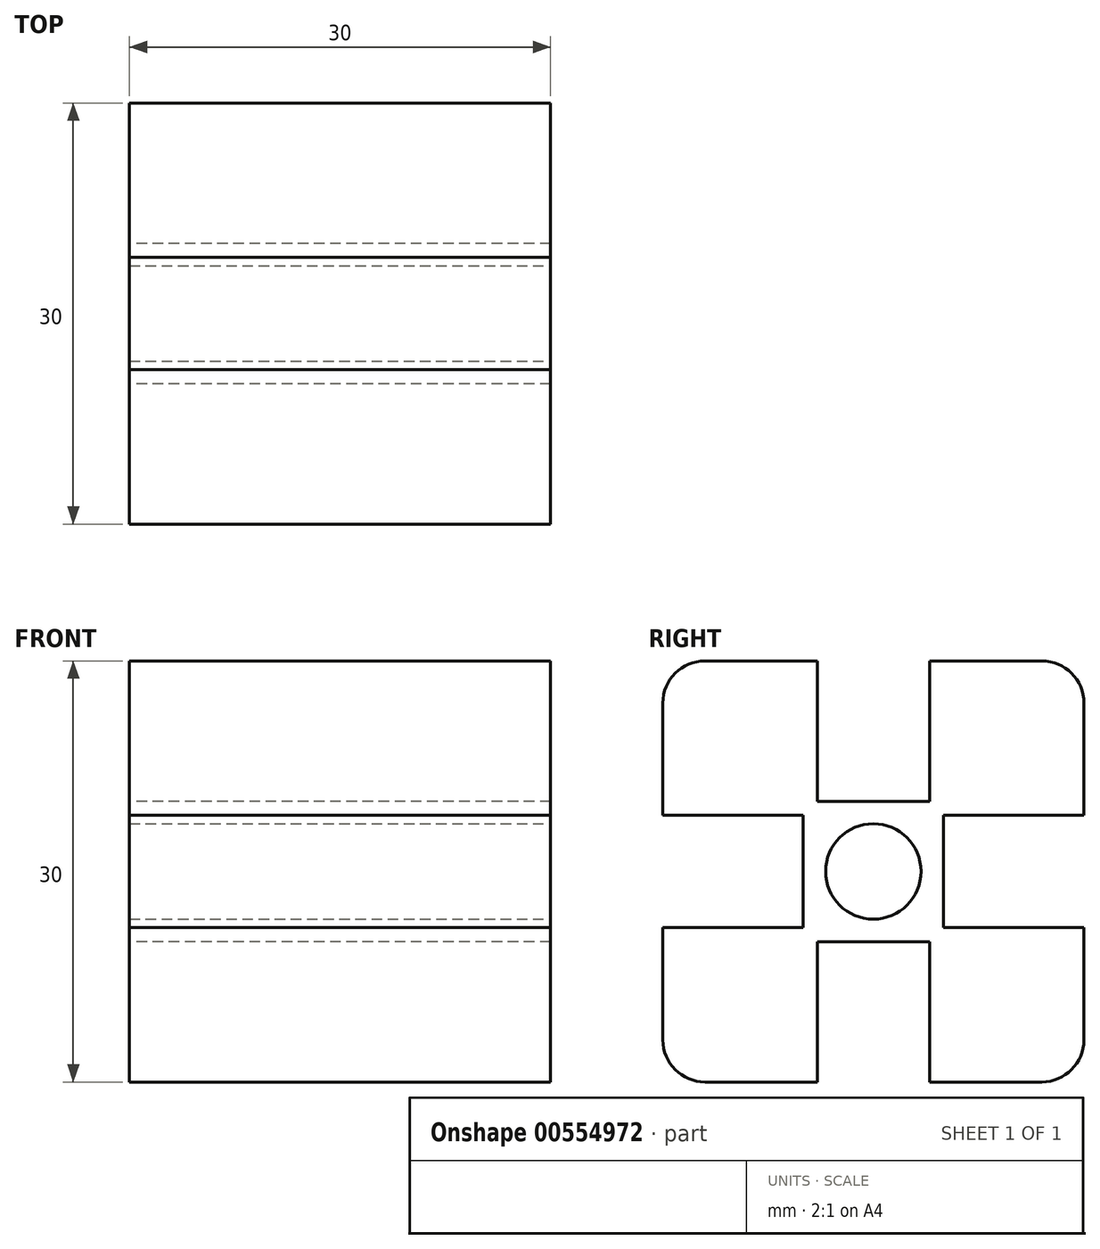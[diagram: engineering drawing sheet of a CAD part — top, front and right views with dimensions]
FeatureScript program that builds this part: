
annotation { "Feature Type Name" : "Feature", "Feature Type Description" : "" }
export const myFeature = defineFeature(function(context is Context, id is Id, definition is map)
    precondition{}
    {
        {
            var Q0;
            Q0=qCreatedBy(makeId("Right.planeOp"),FACE);
            var sketch = newSketch(context, id + "F0", { "sketchPlane" : qUnion([Q0])});
            skLineSegment(sketch, "E0.bottom", {"start": v(15, 30) * mm, "end": v(4, 30) * mm});
            skLineSegment(sketch, "E0.left", {"start": v(15, 30) * mm, "end": v(15, 19) * mm});
            skLineSegment(sketch, "E0.right", {"start": v(-15, 30) * mm, "end": v(-15, 19) * mm});
            skPoint(sketch, "E0.middle", {"position": v(0, 15) * mm});
            skLineSegment(sketch, "E1", {"start": v(-4, 30) * mm, "end": v(-4, 20) * mm});
            skLineSegment(sketch, "E2", {"start": v(-4, 20) * mm, "end": v(4, 20) * mm});
            skLineSegment(sketch, "E3", {"start": v(4, 20) * mm, "end": v(4, 30) * mm});
            skLineSegment(sketch, "E4", {"start": v(-15, 19) * mm, "end": v(-5, 19) * mm});
            skLineSegment(sketch, "E5", {"start": v(-5, 19) * mm, "end": v(-5, 11) * mm});
            skLineSegment(sketch, "E6", {"start": v(-5, 11) * mm, "end": v(-15, 11) * mm});
            skLineSegment(sketch, "E7", {"start": v(15, 19) * mm, "end": v(5, 19) * mm});
            skLineSegment(sketch, "E8", {"start": v(5, 19) * mm, "end": v(5, 11) * mm});
            skLineSegment(sketch, "E9", {"start": v(5, 11) * mm, "end": v(15, 11) * mm});
            skPoint(sketch, "E9.endSnap0", {"position": v(15, 15) * mm});
            skLineSegment(sketch, "E10.trimOffspring", {"start": v(15, 11) * mm, "end": v(15, 0) * mm});
            skLineSegment(sketch, "E11.trimOffspring", {"start": v(-4, 30) * mm, "end": v(-15, 30) * mm});
            skLineSegment(sketch, "E12.trimOffspring", {"start": v(-15, 11) * mm, "end": v(-15, 0) * mm});
            skLineSegment(sketch, "E13", {"start": v(15, 0) * mm, "end": v(4, 0) * mm});
            skLineSegment(sketch, "E14", {"start": v(4, 0) * mm, "end": v(4, 10) * mm});
            skLineSegment(sketch, "E15", {"start": v(4, 10) * mm, "end": v(-4, 10) * mm});
            skLineSegment(sketch, "E16", {"start": v(-4, 10) * mm, "end": v(-4, 0) * mm});
            skLineSegment(sketch, "E17", {"start": v(-4, 0) * mm, "end": v(-15, 0) * mm});
            skPoint(sketch, "E18.MirrorCS.end.orphan", {"position": v(-15, 0) * mm});
            skPoint(sketch, "E18.MirrorCS.start.orphan", {"position": v(-15, -11) * mm});
            skPoint(sketch, "E19.MirrorCS.start.orphan", {"position": v(-5, -11) * mm});
            skPoint(sketch, "E20.MirrorCS.start.orphan", {"position": v(-5, -19) * mm});
            skPoint(sketch, "E21.MirrorCS.start.orphan", {"position": v(-15, -19) * mm});
            skPoint(sketch, "E22.MirrorCS.end.orphan", {"position": v(5, -11) * mm});
            skPoint(sketch, "E22.MirrorCS.start.orphan", {"position": v(5, -19) * mm});
            skPoint(sketch, "E23.MirrorCS.end.orphan", {"position": v(15, -11) * mm});
            skPoint(sketch, "E24.MirrorCS.end.orphan", {"position": v(15, 0) * mm});
            skPoint(sketch, "E25.MirrorCS.start.orphan", {"position": v(15, -19) * mm});
            skPoint(sketch, "E26.MirrorCS.end.orphan", {"position": v(4, -20) * mm});
            skPoint(sketch, "E26.MirrorCS.start.orphan", {"position": v(-4, -20) * mm});
            skPoint(sketch, "E27.MirrorCS.start.orphan", {"position": v(-4, -30) * mm});
            skPoint(sketch, "E28.MirrorCS.end.orphan", {"position": v(4, -30) * mm});
            skPoint(sketch, "E29.MirrorCS.start.orphan", {"position": v(15, -30) * mm});
            skPoint(sketch, "E30.MirrorCS.start.orphan", {"position": v(-15, -30) * mm});
            skSolve(sketch);
        }
        {
            var Q0;
            Q0 = qSketchRegion(id + "F0", true);
            extrude(context, id + "F1", {"entities" : qUnion([Q0]), "depth" : 30 * mm, "offsetDistance" : 25 * mm});
        }
        {
            var Q0;
            Q0=makeQuery(id+"F1.opExtrude","CAP_FACE",FACE,{"disambiguationData":[OSD([sQuery(id+"F0.wireOp",EDGE,"E0.bottom"),sQuery(id+"F0.wireOp",EDGE,"E0.left"),sQuery(id+"F0.wireOp",EDGE,"E0.right"),sQuery(id+"F0.wireOp",EDGE,"E1"),sQuery(id+"F0.wireOp",EDGE,"E2"),sQuery(id+"F0.wireOp",EDGE,"E3"),sQuery(id+"F0.wireOp",EDGE,"E4"),sQuery(id+"F0.wireOp",EDGE,"E5"),sQuery(id+"F0.wireOp",EDGE,"E6"),sQuery(id+"F0.wireOp",EDGE,"E7"),sQuery(id+"F0.wireOp",EDGE,"E8"),sQuery(id+"F0.wireOp",EDGE,"E9"),sQuery(id+"F0.wireOp",EDGE,"E10.trimOffspring"),sQuery(id+"F0.wireOp",EDGE,"E11.trimOffspring"),sQuery(id+"F0.wireOp",EDGE,"E12.trimOffspring"),sQuery(id+"F0.wireOp",EDGE,"E13"),sQuery(id+"F0.wireOp",EDGE,"E14"),sQuery(id+"F0.wireOp",EDGE,"E15"),sQuery(id+"F0.wireOp",EDGE,"E16"),sQuery(id+"F0.wireOp",EDGE,"E17")])],"isStart":false});
            var sketch = newSketch(context, id + "F2", { "sketchPlane" : qUnion([Q0])});
            skCircle(sketch, "E31", {"center": v(0, 15) * mm, "radius": 3.4 * mm});
            skSolve(sketch);
        }
        {
            var Q0;
            Q0 = qSketchRegion(id + "F2", true);
            extrude(context, id + "F3", {"entities" : qUnion([Q0]), "operationType" : NewBodyOperationType.REMOVE, "oppositeDirection" : true, "depth" : 30 * mm, "offsetDistance" : 25 * mm});
        }
        {
            var Q0;
            Q0=makeQuery(id+"F1.opExtrude","SWEPT_EDGE",EDGE,{"disambiguationData":[OSD([sQuery(id+"F0.wireOp",EDGE,"E0.bottom"),sQuery(id+"F0.wireOp",EDGE,"E0.left")])]});
            var Q1;
            Q1=makeQuery(id+"F1.opExtrude","SWEPT_EDGE",EDGE,{"disambiguationData":[OSD([sQuery(id+"F0.wireOp",EDGE,"E12.trimOffspring"),sQuery(id+"F0.wireOp",EDGE,"E17")])]});
            var Q2;
            Q2=makeQuery(id+"F1.opExtrude","SWEPT_EDGE",EDGE,{"disambiguationData":[OSD([sQuery(id+"F0.wireOp",EDGE,"E0.right"),sQuery(id+"F0.wireOp",EDGE,"E11.trimOffspring")])]});
            var Q3;
            Q3=makeQuery(id+"F1.opExtrude","SWEPT_EDGE",EDGE,{"disambiguationData":[OSD([sQuery(id+"F0.wireOp",EDGE,"E10.trimOffspring"),sQuery(id+"F0.wireOp",EDGE,"E13")])]});
            fillet(context, id + "F4", {"entities" : qUnion([Q0, Q1, Q2, Q3]), "radius" : 3 * mm, "tangentPropagation" : true, "allowEdgeOverflow" : false});
        }
    });
